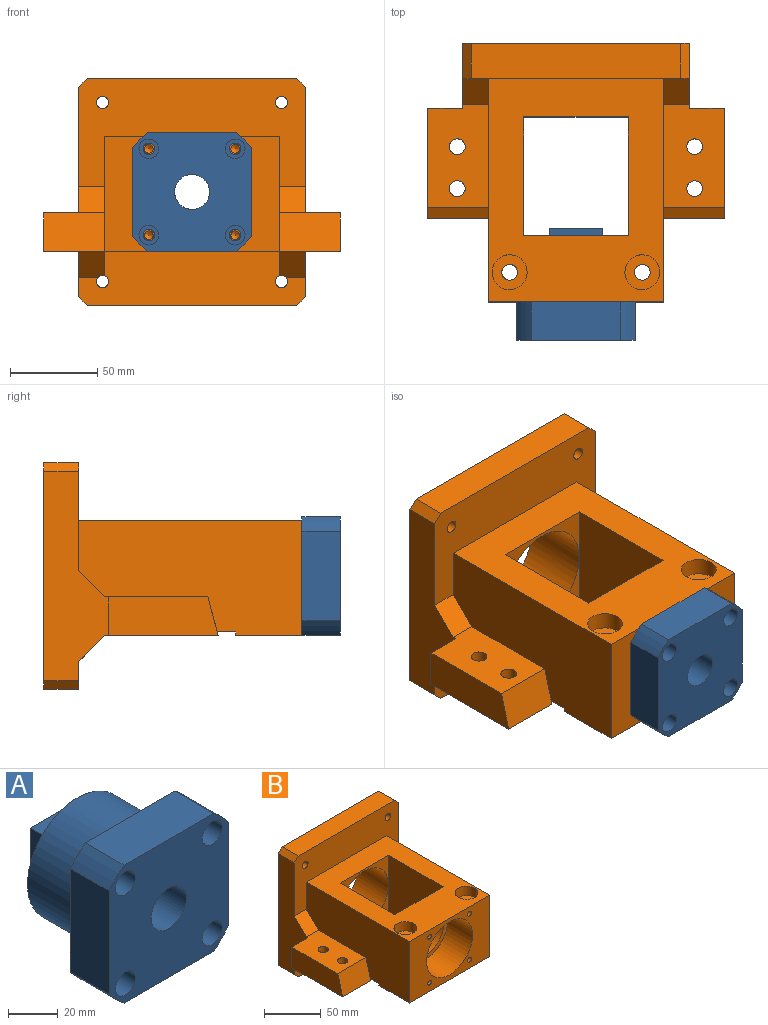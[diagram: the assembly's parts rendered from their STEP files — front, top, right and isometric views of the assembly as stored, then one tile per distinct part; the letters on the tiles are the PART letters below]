
ASSEMBLY  parts=2 mates=1
PART A: 30 faces, bbox 68x64x68 mm
  f0: plane 51x22mm, normal (-1,0,0), area 1122mm2, adj f4,f5,f7,f9
  f1: plane 51x22mm, normal (0,0,-1), area 1122mm2, adj f4,f5,f7,f8
  f2: plane 51x22mm, normal (1,0,0), area 1122mm2, adj f4,f5,f6,f8
  f3: plane 51x22mm, normal (0,0,1), area 1122mm2, adj f4,f5,f6,f9
  f4: plane 68x68mm, normal (0,1,0), area 1804.6mm2, adj f0,f1,f2,f3,f6,f7,f8,f9
  f5: plane 68x68mm, normal (0,-1,0), area 3781.4mm2, adj f0,f1,f2,f3,f6,f7,f8,f9
  f6: cylinder r=42.5mm len=22mm, axis (0,-1,0), area 265.3mm2, adj f2,f3,f4,f5
  f7: cylinder r=42.5mm len=22mm, axis (0,-1,0), area 265.3mm2, adj f0,f1,f4,f5
  f8: cylinder r=42.5mm len=22mm, axis (0,-1,0), area 265.3mm2, adj f1,f2,f4,f5
  f9: cylinder r=42.5mm len=22mm, axis (0,-1,0), area 265.3mm2, adj f0,f3,f4,f5
  f10: cylinder r=28.5mm len=57mm, axis (0,-1,0), area 5372.1mm2, adj f4,f11
  f11: plane 57x57mm, normal (0,1,0), area 1651.8mm2, adj f10,f24,f25,f26,f27
  f12: cylinder r=3.3mm len=12mm, axis (0,-1,0), area 248.8mm2, adj f4,f13
  f13: plane 11.25x11.25mm, normal (0,-1,0), area 65.2mm2, adj f12,f14
  f14: cylinder r=5.62mm len=11.25mm, axis (0,-1,0), area 353.4mm2, adj f5,f13
  f15: cylinder r=3.3mm len=12mm, axis (0,-1,0), area 248.8mm2, adj f4,f16
  f16: plane 11.25x11.25mm, normal (0,-1,0), area 65.2mm2, adj f15,f17
  f17: cylinder r=5.62mm len=11.25mm, axis (0,-1,0), area 353.4mm2, adj f5,f16
  f18: cylinder r=3.3mm len=12mm, axis (0,-1,0), area 248.8mm2, adj f4,f19
  f19: plane 11.25x11.25mm, normal (0,-1,0), area 65.2mm2, adj f18,f20
  f20: cylinder r=5.62mm len=11.25mm, axis (0,-1,0), area 353.4mm2, adj f5,f19
  f21: cylinder r=3.3mm len=12mm, axis (0,-1,0), area 248.8mm2, adj f4,f22
  f22: plane 11.25x11.25mm, normal (0,-1,0), area 65.2mm2, adj f21,f23
  f23: cylinder r=5.62mm len=11.25mm, axis (0,-1,0), area 353.4mm2, adj f5,f22
  f24: plane 30x12mm, normal (1,0,0), area 360mm2, adj f11,f25,f27,f28
  f25: plane 30x12mm, normal (0,0,-1), area 360mm2, adj f11,f24,f26,f28
  f26: plane 30x12mm, normal (-1,0,0), area 360mm2, adj f11,f25,f27,f28
  f27: plane 30x12mm, normal (0,0,1), area 360mm2, adj f11,f24,f26,f28
  f28: plane 30x30mm, normal (0,1,0), area 585.8mm2, adj f24,f25,f26,f27,f29
  f29: cylinder r=10mm len=64mm, axis (0,-1,0), area 4021.2mm2, adj f5,f28
PART B: 66 faces, bbox 170x148x130 mm
  f0: plane 100x66mm, normal (0,1,0), area 2230.4mm2, adj f10,f11,f13,f14,f15,f16,f30,f65
  f1: plane 120x20mm, normal (0,0,-1), area 2400mm2, adj f37,f39,f48,f50
  f2: plane 120x20mm, normal (0,0,1), area 2400mm2, adj f38,f40,f48,f49
  f3: plane 120x37mm, normal (-1,0,0), area 2999mm2, adj f9,f21,f27,f37,f38,f48,f49,f50
  f4: plane 120x37mm, normal (1,0,0), area 2999mm2, adj f19,f20,f29,f39,f40,f48,f49,f50
  f5: cylinder r=4.5mm len=56mm, axis (0,0,1), area 1583.4mm2, adj f30,f45
  f6: cylinder r=4.5mm len=56mm, axis (0,0,1), area 1583.4mm2, adj f30,f43
  f7: plane 63x22mm, normal (1,0,0), area 1321.2mm2, adj f19,f20,f29,f36
  f8: plane 63x22mm, normal (-1,0,0), area 1321.2mm2, adj f9,f21,f27,f35
  f9: plane 59.11x35mm, normal (0,0,1), area 1901.4mm2, adj f3,f8,f11,f21,f31,f32,f35,f53
  f10: plane 100x90mm, normal (0,0,-1), area 4920mm2, adj f0,f11,f13,f15,f16,f17,f26,f28
  f11: plane 128x66mm, normal (-1,0,0), area 6619.8mm2, adj f0,f9,f10,f14,f30,f35,f41,f49
  f12: plane 60x32mm, normal (0,-1,0), area 506.3mm2, adj f14,f15,f16,f18
  f13: plane 128x66mm, normal (1,0,0), area 6619.8mm2, adj f0,f10,f14,f19,f30,f36,f41,f49
  f14: plane 128x100mm, normal (0,0,1), area 8091.7mm2, adj f0,f11,f12,f13,f15,f16,f41,f42
  f15: plane 68x64mm, normal (1,0,0), area 4352mm2, adj f0,f10,f12,f14,f17
  f16: plane 68x64mm, normal (-1,0,0), area 4352mm2, adj f0,f10,f12,f14,f17
  f17: plane 60x32mm, normal (0,-1,0), area 506.3mm2, adj f10,f15,f16,f18
  f18: cylinder r=30mm len=60mm, axis (0,1,0), area 7162.8mm2, adj f12,f17,f46
  f19: plane 59.11x35mm, normal (0,0,1), area 1901.4mm2, adj f4,f7,f13,f20,f33,f34,f36,f54
  f20: plane 22x20mm, normal (0,1,0), area 440mm2, adj f4,f7,f19,f29
  f21: plane 22x20mm, normal (0,1,0), area 440mm2, adj f3,f8,f9,f27
  f22: cylinder r=3.5mm len=20mm, axis (0,1,0), area 439.8mm2, adj f48,f49
  f23: cylinder r=3.5mm len=21.23mm, axis (0,1,0), area 443.8mm2, adj f26,f48,f50,f52
  f24: cylinder r=3.5mm len=21.23mm, axis (0,1,0), area 443.8mm2, adj f28,f48,f50,f51
  f25: cylinder r=3.5mm len=20mm, axis (0,1,0), area 439.8mm2, adj f48,f49
  f26: plane 80x16mm, normal (1,0,0), area 271.5mm2, adj f10,f23,f27,f35,f50,f52
  f27: plane 65x35mm, normal (0,0,-1), area 2107.8mm2, adj f3,f8,f21,f26,f31,f32,f35,f52
  f28: plane 80x16mm, normal (-1,0,0), area 271.5mm2, adj f10,f24,f29,f36,f50,f51
  f29: plane 65x35mm, normal (0,0,-1), area 2107.8mm2, adj f4,f7,f20,f28,f33,f34,f36,f51
  f30: plane 100x38mm, normal (0,0,-1), area 3672.8mm2, adj f0,f5,f6,f11,f13,f41
  f31: cylinder r=4.5mm len=22mm, axis (0,0,-1), area 622mm2, adj f9,f27
  f32: cylinder r=4.5mm len=22mm, axis (0,0,-1), area 622mm2, adj f9,f27
  f33: cylinder r=4.5mm len=22mm, axis (0,0,-1), area 622mm2, adj f19,f29
  f34: cylinder r=4.5mm len=22mm, axis (0,0,-1), area 622mm2, adj f19,f29
  f35: plane 35x22mm, normal (0,-0.97,0.26), area 797.2mm2, adj f8,f9,f11,f26,f27
  f36: plane 35x22mm, normal (0,-0.97,0.26), area 797.2mm2, adj f7,f13,f19,f28,f29
  f37: plane 20x5mm, normal (-0.71,0,-0.71), area 141.4mm2, adj f1,f3,f48,f50
  f38: plane 20x5mm, normal (-0.71,0,0.71), area 141.4mm2, adj f2,f3,f48,f49
  f39: plane 20x5mm, normal (0.71,0,-0.71), area 141.4mm2, adj f1,f4,f48,f50
  f40: plane 20x5mm, normal (0.71,0,0.71), area 141.4mm2, adj f2,f4,f48,f49
  f41: plane 100x66mm, normal (0,-1,0), area 3969.7mm2, adj f11,f13,f14,f30,f56,f57,f59,f61
  f42: cylinder r=10mm len=20mm, axis (0,0,1), area 628.3mm2, adj f14,f43
  f43: plane 20x20mm, normal (0,0,1), area 250.5mm2, adj f6,f42
  f44: cylinder r=10mm len=20mm, axis (0,0,1), area 628.3mm2, adj f14,f45
  f45: plane 20x20mm, normal (0,0,1), area 250.5mm2, adj f5,f44
  f46: plane 110x110mm, normal (0,1,0), area 6675.9mm2, adj f18,f47
  f47: cylinder r=55mm len=110mm, axis (0,-1,0), area 1382.3mm2, adj f46,f48
  f48: plane 130x130mm, normal (0,1,0), area 7192.7mm2, adj f1,f2,f3,f4,f22,f23,f24,f25
  f49: plane 130x62mm, normal (0,-1,0), area 5058mm2, adj f2,f3,f4,f11,f13,f14,f22,f25
  f50: plane 130x33mm, normal (0,-1,0), area 3685.5mm2, adj f1,f3,f4,f10,f23,f24,f26,f28
  f51: plane 15x15mm, normal (0,-0.71,-0.71), area 312.9mm2, adj f4,f24,f28,f29,f50
  f52: plane 15x15mm, normal (0,-0.71,-0.71), area 312.9mm2, adj f3,f23,f26,f27,f50
  f53: plane 15x15mm, normal (0,-0.71,0.71), area 318.2mm2, adj f3,f9,f11,f49
  f54: plane 15x15mm, normal (0,-0.71,0.71), area 318.2mm2, adj f4,f13,f19,f49
  f55: plane 57x57mm, normal (0,-1,0), area 742.2mm2, adj f56,f65
  f56: cylinder r=28.5mm len=57mm, axis (0,-1,0), area 5551.2mm2, adj f41,f55
  f57: cylinder r=2.5mm len=25mm, axis (0,-1,0), area 392.7mm2, adj f41,f58
  f58: cone r=0mm half-angle=59deg, axis (0,-1,0), area 22.9mm2, adj f57
  f59: cylinder r=2.5mm len=25mm, axis (0,-1,0), area 392.7mm2, adj f41,f60
  f60: cone r=0mm half-angle=59deg, axis (0,-1,0), area 22.9mm2, adj f59
  f61: cylinder r=2.5mm len=25mm, axis (0,-1,0), area 392.7mm2, adj f41,f62
  f62: cone r=0mm half-angle=59deg, axis (0,-1,0), area 22.9mm2, adj f61
  f63: cylinder r=2.5mm len=25mm, axis (0,-1,0), area 392.7mm2, adj f41,f64
  f64: cone r=0mm half-angle=59deg, axis (0,-1,0), area 22.9mm2, adj f63
  f65: cylinder r=24mm len=48mm, axis (0,-1,0), area 1055.6mm2, adj f0,f55
PLACE A t=(-4.34,-93.59,7.37)mm
PLACE B t=(-4.34,55.41,7.37)mm
MATE fastened A.f6 <-> B.f18  axis (0,1,0) through (-4.34,-71.59,7.37)mm
